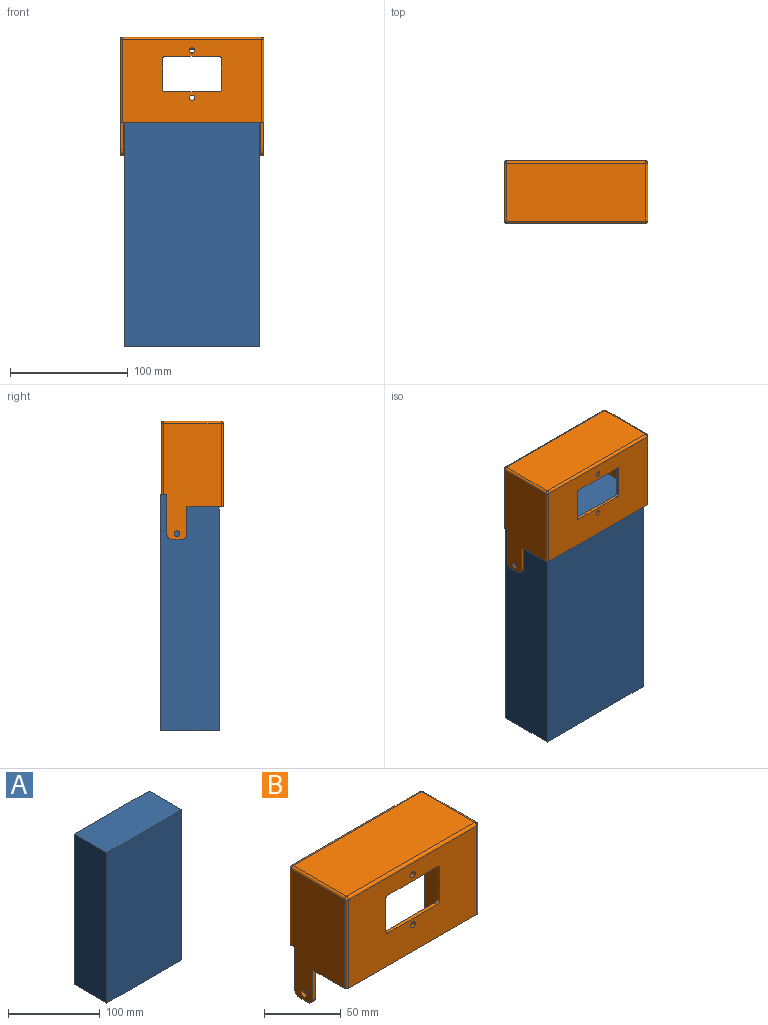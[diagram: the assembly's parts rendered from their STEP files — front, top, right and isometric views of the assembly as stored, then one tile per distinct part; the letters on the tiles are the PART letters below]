
ASSEMBLY  parts=2 mates=1
PART A: 6 faces, bbox 115x50x200 mm
  f0: plane 200x115mm, normal (0,1,0), area 23000mm2, adj f1,f3,f4,f5
  f1: plane 200x50mm, normal (-1,0,0), area 10000mm2, adj f0,f2,f4,f5
  f2: plane 200x115mm, normal (0,-1,0), area 23000mm2, adj f1,f3,f4,f5
  f3: plane 200x50mm, normal (1,0,0), area 10000mm2, adj f0,f2,f4,f5
  f4: plane 115x50mm, normal (0,0,1), area 5750mm2, adj f0,f1,f2,f3
  f5: plane 115x50mm, normal (0,0,-1), area 5750mm2, adj f0,f1,f2,f3
PART B: 54 faces, bbox 122x53x100.5 mm
  f0: plane 7x5mm, normal (0,0,-1), area 22.9mm2, adj f1,f2,f4,f8,f24,f31,f45
  f1: plane 118x60.5mm, normal (0,1,0), area 1994mm2, adj f0,f3,f31,f34,f39,f40,f41,f42
  f2: plane 117x60mm, normal (0,-1,0), area 1875mm2, adj f0,f3,f8,f10,f11,f39,f40,f41
  f3: plane 7x5mm, normal (0,0,-1), area 22.9mm2, adj f1,f2,f6,f10,f27,f34,f44
  f4: plane 98.5x49mm, normal (-1,0,0), area 3870.1mm2, adj f0,f22,f23,f24,f25,f30,f31,f32
  f5: plane 118x70.5mm, normal (0,-1,0), area 6792mm2, adj f12,f13,f14,f15,f16,f17,f18,f19
  f6: plane 98.5x49mm, normal (1,0,0), area 3870.1mm2, adj f3,f22,f26,f27,f28,f29,f33,f34
  f7: plane 118x49mm, normal (0,0,1), area 5782mm2, adj f46,f49,f50,f53
  f8: plane 98x48mm, normal (1,0,0), area 3780.6mm2, adj f0,f2,f9,f11,f22,f23,f24,f25
  f9: plane 117x70mm, normal (0,1,0), area 6663mm2, adj f8,f10,f11,f12,f13,f14,f15,f16
  f10: plane 98x48mm, normal (-1,0,0), area 3780.6mm2, adj f2,f3,f9,f11,f22,f26,f27,f28
  f11: plane 117x48mm, normal (0,0,-1), area 5616mm2, adj f2,f8,f9,f10
  f12: plane 26x2.5mm, normal (1,0,0), area 65mm2, adj f5,f9,f16,f19
  f13: plane 46x2.5mm, normal (0,0,1), area 115mm2, adj f5,f9,f16,f17
  f14: plane 26x2.5mm, normal (-1,0,0), area 65mm2, adj f5,f9,f17,f18
  f15: plane 46x2.5mm, normal (0,0,-1), area 115mm2, adj f5,f9,f18,f19
  f16: cylinder r=2mm len=2.5mm, axis (0,1,0), area 7.9mm2, adj f5,f9,f12,f13
  f17: cylinder r=2mm len=2.5mm, axis (0,-1,0), area 7.9mm2, adj f5,f9,f13,f14
  f18: cylinder r=2mm len=2.5mm, axis (0,1,0), area 7.9mm2, adj f5,f9,f14,f15
  f19: cylinder r=2mm len=2.5mm, axis (0,-1,0), area 7.9mm2, adj f5,f9,f12,f15
  f20: cylinder r=2.2mm len=4.4mm, axis (0,-1,0), area 34.6mm2, adj f5,f9
  f21: cylinder r=2.2mm len=4.4mm, axis (0,-1,0), area 34.6mm2, adj f5,f9
  f22: plane 122x31mm, normal (0,0,-1), area 445.8mm2, adj f4,f5,f6,f8,f9,f10,f23,f26
  f23: plane 23x2.5mm, normal (0,-1,0), area 57.5mm2, adj f4,f8,f22,f35
  f24: plane 33x2.5mm, normal (0,1,0), area 82.5mm2, adj f0,f4,f8,f36
  f25: plane 7x2.5mm, normal (0,0,-1), area 17.5mm2, adj f4,f8,f35,f36
  f26: plane 23x2.5mm, normal (0,-1,0), area 57.5mm2, adj f6,f10,f22,f38
  f27: plane 33x2.5mm, normal (0,1,0), area 82.5mm2, adj f3,f6,f10,f37
  f28: plane 7x2.5mm, normal (0,0,-1), area 17.5mm2, adj f6,f10,f37,f38
  f29: cylinder r=2.5mm len=5mm, axis (1,0,0), area 39.3mm2, adj f6,f10
  f30: cylinder r=2.5mm len=5mm, axis (1,0,0), area 39.3mm2, adj f4,f8
  f31: cylinder r=2mm len=60.5mm, axis (0,0,1), area 190.1mm2, adj f0,f1,f4,f47
  f32: cylinder r=2mm len=70.5mm, axis (0,0,-1), area 221.5mm2, adj f4,f5,f22,f51
  f33: cylinder r=2mm len=70.5mm, axis (0,0,1), area 221.5mm2, adj f5,f6,f22,f52
  f34: cylinder r=2mm len=60.5mm, axis (0,0,-1), area 190.1mm2, adj f1,f3,f6,f48
  f35: cylinder r=5mm len=5mm, axis (1,0,0), area 19.6mm2, adj f4,f8,f23,f25
  f36: cylinder r=5mm len=5mm, axis (-1,0,0), area 19.6mm2, adj f4,f8,f24,f25
  f37: cylinder r=5mm len=5mm, axis (-1,0,0), area 19.6mm2, adj f6,f10,f27,f28
  f38: cylinder r=5mm len=5mm, axis (1,0,0), area 19.6mm2, adj f6,f10,f26,f28
  f39: plane 42.5x2.5mm, normal (-1,0,0), area 106.2mm2, adj f1,f2,f43,f44
  f40: plane 42.5x2.5mm, normal (1,0,0), area 106.2mm2, adj f1,f2,f42,f45
  f41: plane 88x2.5mm, normal (0,0,-1), area 220mm2, adj f1,f2,f42,f43
  f42: cylinder r=5mm len=5mm, axis (0,1,0), area 19.6mm2, adj f1,f2,f40,f41
  f43: cylinder r=5mm len=5mm, axis (0,-1,0), area 19.6mm2, adj f1,f2,f39,f41
  f44: cylinder r=5mm len=5mm, axis (0,-1,0), area 19.6mm2, adj f1,f2,f3,f39
  f45: cylinder r=5mm len=5mm, axis (0,1,0), area 19.6mm2, adj f0,f1,f2,f40
  f46: cylinder r=2mm len=118mm, axis (1,0,0), area 370.7mm2, adj f1,f7,f47,f48
  f47: sphere r=2mm, area 6.3mm2, adj f31,f46,f49
  f48: sphere r=2mm, area 6.3mm2, adj f34,f46,f50
  f49: cylinder r=2mm len=49mm, axis (0,1,0), area 153.9mm2, adj f4,f7,f47,f51
  f50: cylinder r=2mm len=49mm, axis (0,-1,0), area 153.9mm2, adj f6,f7,f48,f52
  f51: sphere r=2mm, area 6.3mm2, adj f32,f49,f53
  f52: sphere r=2mm, area 6.3mm2, adj f33,f50,f53
  f53: cylinder r=2mm len=118mm, axis (-1,0,0), area 370.7mm2, adj f5,f7,f51,f52
PLACE A at identity
PLACE B t=(0,-2,200)mm
MATE fastened B.f3 <-> A.f4  axis (0,0,-1) through (0,-2,200)mm
